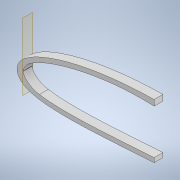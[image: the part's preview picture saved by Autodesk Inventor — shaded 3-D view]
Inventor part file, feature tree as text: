
AUTODESK INVENTOR PART (.ipt)
format: ipt  version: 2022.3 (Build 263350000, 350)  size: 482,816 bytes
history: native  units: mm
features: sketch x6, extrude x5, thicken_offset x3, projected_geometry x2, shell x1, plane x1, other x1
ambient origin geometry x8: Origin, YZ Plane, XZ Plane, XY Plane, X Axis, Y Axis, Z Axis, Center Point
bodies: Solid1 (feature_tree)
feature tree (19):
  extrude  "Extrusion1"  Depth=10.0mm
  shell  "Shell1"  Thickness=1.0mm
  thicken_offset  "Thicken1"
  extrude  "Extrusion27"  TaperAngle=0.0deg  [1 undecoded]
  thicken_offset  "Thicken3"
  extrude  "Extrusion29"  Depth=20.0mm
  plane  "Work Plane5"
  other  "Bend Part2"
  thicken_offset  "Thicken5"
  extrude  "Extrusion30"  Depth=10.0mm TaperAngle=0.0deg
  extrude  "Extrusion31"  Depth=10.0mm
  sketch  "Sketch3"  dims[d0=10.0mm d1=0.0mm d2=3.0mm d159=1.0mm d160=2.0mm]
  sketch  "Sketch48"  dims[d236=190.0mm d237=0.0mm d238=0.0mm]
  sketch  "Sketch55"  dims[d249=2.0mm d250=1.0mm d254=20.0mm]
  projected_geometry  "Projected Loop32"
  sketch  "Sketch57"  dims[d255=8.0mm d256=10.0mm d257=0.0mm]
  sketch  "Sketch58"  dims[d262=10.0mm d263=0.349066mm d264=1.0mm]
  projected_geometry  "Projected Loop34"
  sketch  "Sketch59"  dims[d265=1.0mm d268=100.0mm d269=5.0mm d270=10.0mm d271=0.0mm d272=150.0mm d273=100.0mm d274=0.0mm]
note: 1 required parameter value undecoded (feature->parameter linkage not recoverable at this tier; creation-order binding heuristic only, values carry confidence <= 0.55)
